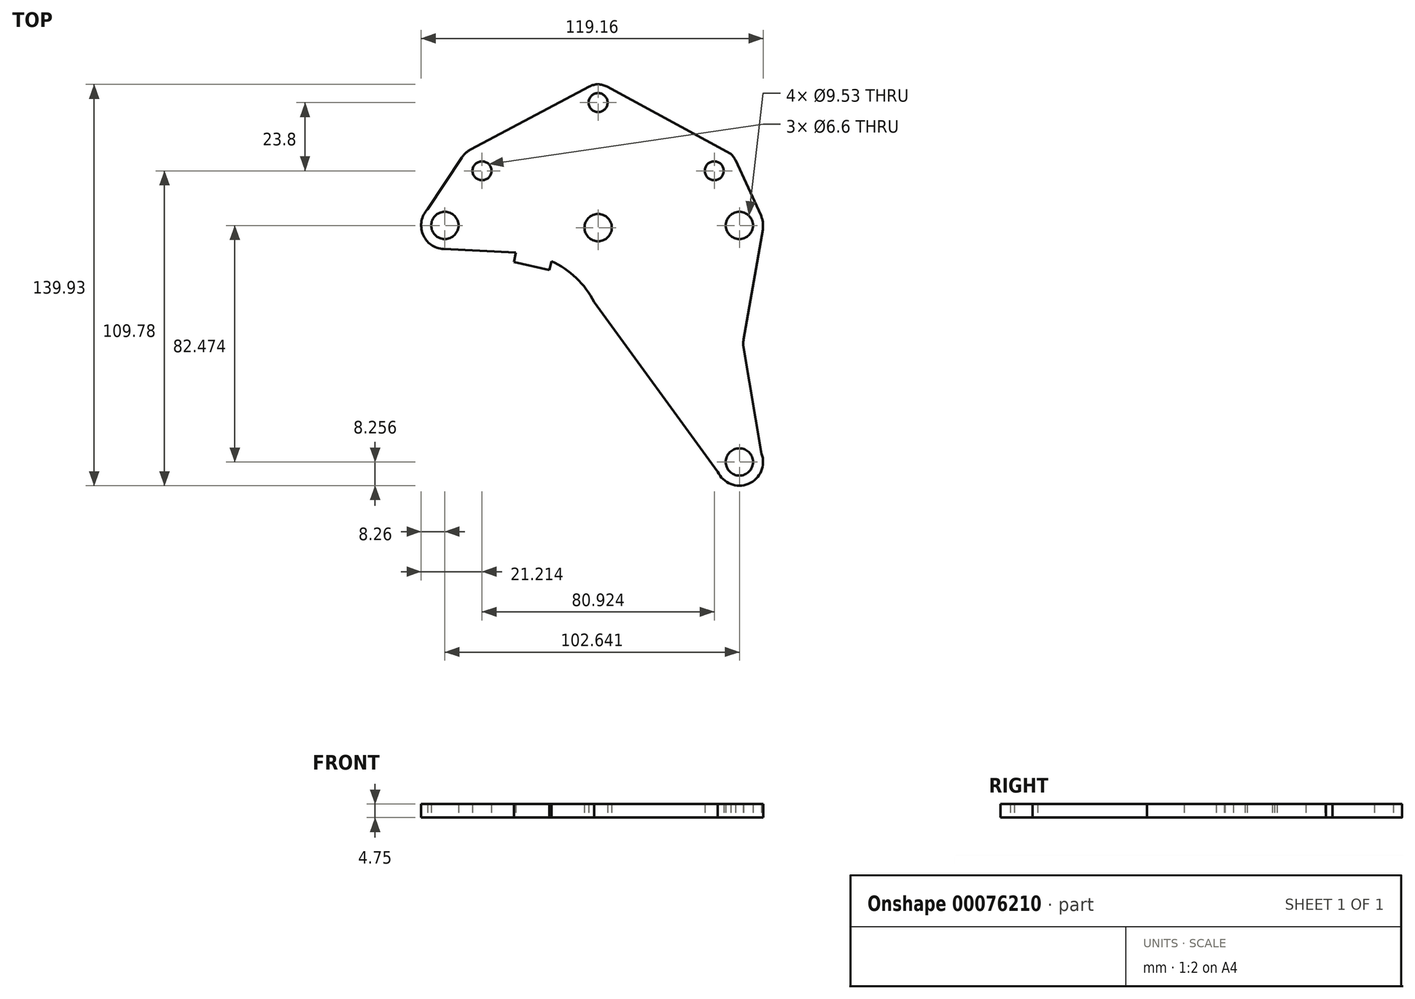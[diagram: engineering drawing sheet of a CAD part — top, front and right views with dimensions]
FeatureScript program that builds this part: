
annotation { "Feature Type Name" : "Feature", "Feature Type Description" : "" }
export const myFeature = defineFeature(function(context is Context, id is Id, definition is map)
    precondition{}
    {
        {
            var Q0;
            Q0=qCreatedBy(makeId("Top.planeOp"),FACE);
            var sketch = newSketch(context, id + "F0", { "sketchPlane" : qUnion([Q0])});
            skLineSegment(sketch, "E0", {"start": v(-88.85, 0) * mm, "end": v(105.53, 0) * mm, "construction": true});
            skLineSegment(sketch, "E1", {"start": v(-55.5, -34.96) * mm, "end": v(-55.5, 26.62) * mm, "construction": true});
            skLineSegment(sketch, "E2", {"start": v(47.15, 34.32) * mm, "end": v(47.15, -8.26) * mm, "construction": true});
            skLineSegment(sketch, "E3", {"start": v(-2.07, 20.88) * mm, "end": v(-2.07, -30.64) * mm, "construction": true});
            skLineSegment(sketch, "E4", {"start": v(-11.38, -0.76) * mm, "end": v(12.27, -0.76) * mm, "construction": true});
            skLineSegment(sketch, "E5", {"start": v(33.86, -82.47) * mm, "end": v(56.18, -82.47) * mm, "construction": true});
            skLineSegment(sketch, "E6", {"start": v(47.15, -34) * mm, "end": v(47.15, -36.25) * mm, "construction": true});
            skCircle(sketch, "E7", {"center": v(-55.5, 0) * mm, "radius": 4.76 * mm});
            skCircle(sketch, "E8", {"center": v(-2.07, -0.76) * mm, "radius": 4.76 * mm});
            skCircle(sketch, "E9", {"center": v(47.15, 0) * mm, "radius": 4.76 * mm});
            skCircle(sketch, "E10", {"center": v(47.15, -82.47) * mm, "radius": 4.76 * mm});
            skLineSegment(sketch, "E11", {"start": v(-73.98, 19.05) * mm, "end": v(99.09, 19.05) * mm, "construction": true});
            skLineSegment(sketch, "E12", {"start": v(-77.3, 42.85) * mm, "end": v(62.65, 42.85) * mm, "construction": true});
            skLineSegment(sketch, "E13", {"start": v(-2.07, 15.97) * mm, "end": v(-2.07, 64.55) * mm, "construction": true});
            skLineSegment(sketch, "E14", {"start": v(-42.54, 49.45) * mm, "end": v(-42.54, 30.41) * mm, "construction": true});
            skLineSegment(sketch, "E15", {"start": v(38.39, 49.12) * mm, "end": v(38.39, 29.1) * mm, "construction": true});
            skLineSegment(sketch, "E16", {"start": v(-42.54, 33.37) * mm, "end": v(-42.54, 13.18) * mm, "construction": true});
            skLineSegment(sketch, "E17", {"start": v(38.39, 31.24) * mm, "end": v(38.39, 14.5) * mm, "construction": true});
            skCircle(sketch, "E18", {"center": v(-2.07, 42.85) * mm, "radius": 3.3 * mm});
            skCircle(sketch, "E19", {"center": v(-42.54, 19.05) * mm, "radius": 3.3 * mm});
            skCircle(sketch, "E20", {"center": v(38.39, 19.05) * mm, "radius": 3.3 * mm});
            skArc(sketch, "E21", {"start": v(0.96, 48.43) * mm, "mid": v(-2.04, 49.2) * mm, "end": v(-5.05, 48.46) * mm});
            skArc(sketch, "E22", {"start": v(45.77, 22.74) * mm, "mid": v(45.07, 23.9) * mm, "end": v(44.19, 24.93) * mm});
            skArc(sketch, "E23", {"start": v(55.28, -1.41) * mm, "mid": v(55.34, 1.07) * mm, "end": v(54.65, 3.45) * mm});
            skArc(sketch, "E24", {"start": v(-61.47, 5.7) * mm, "mid": v(-63.16, -3.06) * mm, "end": v(-55.9, -8.24) * mm});
            skArc(sketch, "E25", {"start": v(39.62, -85.85) * mm, "mid": v(50.32, -90.1) * mm, "end": v(54.86, -79.53) * mm});
            skLineSegment(sketch, "E26", {"start": v(-89.34, -41.25) * mm, "end": v(99.02, -41.25) * mm, "construction": true});
            skArc(sketch, "E27", {"start": v(-3.48, -26.69) * mm, "mid": v(-9.72, -18.33) * mm, "end": v(-18.34, -12.44) * mm});
            skLineSegment(sketch, "E28", {"start": v(56.68, -29.06) * mm, "end": v(56.68, -56.1) * mm, "construction": true});
            skLineSegment(sketch, "E29", {"start": v(-55.9, -8.24) * mm, "end": v(-30.7, -9.5) * mm});
            skLineSegment(sketch, "E30", {"start": v(-3.48, -26.69) * mm, "end": v(39.62, -85.85) * mm});
            skLineSegment(sketch, "E31", {"start": v(44.19, 24.93) * mm, "end": v(0.96, 48.43) * mm});
            skArc(sketch, "E32", {"start": v(-46.48, 26.48) * mm, "mid": v(-48.19, 25.28) * mm, "end": v(-49.55, 23.7) * mm});
            skLineSegment(sketch, "E33", {"start": v(-5.05, 48.46) * mm, "end": v(-46.48, 26.48) * mm});
            skLineSegment(sketch, "E34", {"start": v(-61.47, 5.7) * mm, "end": v(-49.55, 23.7) * mm});
            skLineSegment(sketch, "E35", {"start": v(45.77, 22.74) * mm, "end": v(54.65, 3.45) * mm});
            skLineSegment(sketch, "E36", {"start": v(-31.7, -41.25) * mm, "end": v(-22.65, -3.1) * mm, "construction": true});
            skLineSegment(sketch, "E37", {"start": v(-30.88, -12.73) * mm, "end": v(-27.17, -13.6) * mm, "construction": true});
            skPoint(sketch, "E37.endSnap0", {"position": v(-27.17, -22.18) * mm});
            skLineSegment(sketch, "E38", {"start": v(-31.46, -12.73) * mm, "end": v(-30.7, -9.5) * mm});
            skLineSegment(sketch, "E39", {"start": v(-27.17, -13.6) * mm, "end": v(-25.25, -14.06) * mm, "construction": true});
            skLineSegment(sketch, "E40", {"start": v(-25.25, -14.06) * mm, "end": v(-20.81, -15.11) * mm, "construction": true});
            skLineSegment(sketch, "E41", {"start": v(-19.07, -15.53) * mm, "end": v(-18.34, -12.44) * mm});
            skLineSegment(sketch, "E42", {"start": v(-19.07, -15.53) * mm, "end": v(-31.46, -12.73) * mm});
            skLineSegment(sketch, "E43.trimOffspring", {"start": v(47.15, -41.25) * mm, "end": v(47.15, -84.04) * mm, "construction": true});
            skArc(sketch, "E44", {"start": v(48.64, -39.68) * mm, "mid": v(48.49, -41.15) * mm, "end": v(48.6, -42.62) * mm});
            skLineSegment(sketch, "E45", {"start": v(54.86, -79.53) * mm, "end": v(48.6, -42.62) * mm});
            skLineSegment(sketch, "E46", {"start": v(48.64, -39.68) * mm, "end": v(55.28, -1.41) * mm});
            skPoint(sketch, "E47.orphan", {"position": v(0, 48.95) * mm});
            skPoint(sketch, "E48.trimOffspring.end.orphan", {"position": v(-27.17, 5.37) * mm});
            skSolve(sketch);
        }
        {
            var Q0;
            Q0=makeQuery(id+"F0.imprint","IMPRINT",FACE,{"disambiguationData":[TD([[makeQuery(id+"F0.imprint","IMPRINT",EDGE,{"derivedFrom":sQuery(id+"F0.wireOp",EDGE,"E7")}),-1.0]])]});
            extrude(context, id + "F1", {"entities" : qUnion([Q0]), "depth" : 4.75 * mm});
        }
    });
